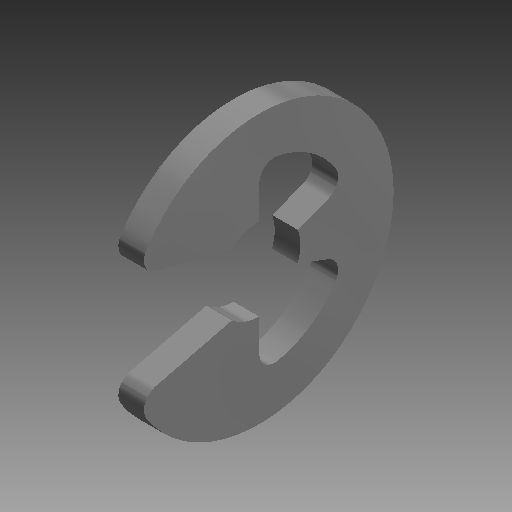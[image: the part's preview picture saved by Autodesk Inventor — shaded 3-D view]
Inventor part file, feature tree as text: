
AUTODESK INVENTOR PART (.ipt)
format: ipt  version: 2019 (Build 230136000, 136)  size: 90,624 bytes
history: native  units: mm (DEFAULTED — no unit token found)
features: fillet x1
ambient origin geometry x8: Origin, YZ Plane, XZ Plane, XY Plane, X Axis, Y Axis, Z Axis, Center Point
bodies: Solid1 (feature_tree)
feature tree (1):
  fillet  "Fillet1"  [1 undecoded]
note: 1 required parameter value undecoded (feature->parameter linkage not recoverable at this tier; creation-order binding heuristic only, values carry confidence <= 0.55)
